FCSTD DOCUMENT  (FreeCAD 0.22R33909 (Git))
Label: milling_vacuum
License: All rights reserved
LicenseURL: http://en.wikipedia.org/wiki/All_rights_reserved
objects: Sketcher::SketchObject×2, PartDesign::Body×1
note: 3 computed .brp shape members not serialized (recipe doc carries the construction recipe); baked Part::Feature solids carry a one-line shape summary decoded from their .brp

FEATURE [Sketcher::SketchObject] Sketch
  FullyConstrained = true
  MapMode = 5
  Support = -> [XY_Plane]
  sketch-geometry (1):
    g0: Circle CenterX=0 CenterY=0 CenterZ=0 NormalX=0 NormalY=0 NormalZ=1 AngleXU=0 Radius=38.5
  constraints (2):
    c: Coincident(g0,g-1)
    c: Diameter(g0) = 77
FEATURE [Sketcher::SketchObject] Sketch001
  AttachmentOffset = pos=(0,0,46) rot=(0,0,1;0rad)
  FullyConstrained = true
  MapMode = 5
  Placement = pos=(0,-46,-1.02e-14) rot=(1,0,0;1.5708rad)
  Support = -> [XZ_Plane]
  sketch-geometry (8):
    g0: ArcOfCircle CenterX=61 CenterY=12 CenterZ=0 NormalX=0 NormalY=0 NormalZ=1 AngleXU=0 Radius=3 StartAngle=3.14159 EndAngle=6.28319
    g1: ArcOfCircle CenterX=61 CenterY=72 CenterZ=0 NormalX=0 NormalY=0 NormalZ=1 AngleXU=0 Radius=3 StartAngle=0 EndAngle=3.14159
    g2: LineSegment StartX=64 StartY=12 StartZ=0 EndX=64 EndY=72 EndZ=0
    g3: LineSegment StartX=58 StartY=72 StartZ=0 EndX=58 EndY=12 EndZ=0
    g4: ArcOfCircle CenterX=-61 CenterY=12 CenterZ=0 NormalX=0 NormalY=0 NormalZ=1 AngleXU=0 Radius=3 StartAngle=3.14159 EndAngle=6.28319
    g5: ArcOfCircle CenterX=-61 CenterY=72 CenterZ=0 NormalX=0 NormalY=0 NormalZ=1 AngleXU=0 Radius=3 StartAngle=1.5e-15 EndAngle=3.14159
    g6: LineSegment StartX=-58 StartY=12 StartZ=0 EndX=-58 EndY=72 EndZ=0
    g7: LineSegment StartX=-64 StartY=72 StartZ=0 EndX=-64 EndY=12 EndZ=0
  constraints (18):
    c: Tangent(g0,g2) = -1.5708
    c: Tangent(g2,g1) = -1.5708
    c: Tangent(g1,g3) = -1.5708
    c: Tangent(g3,g0) = -1.5708
    c: Equal(g0,g1)
    c: Vertical(g2)
    c: Tangent(g4,g6) = -1.5708
    c: Tangent(g6,g5) = -1.5708
    c: Tangent(g5,g7) = -1.5708
    c: Tangent(g7,g4) = -1.5708
    c: Equal(g4,g5)
    c: Equal(g4,g0)
    c: Symmetric(g4,g0,g-2)
    c: Symmetric(g5,g1,g-2)
    c: DistanceX(g4,g0) = 122
    c: Diameter(g0) = 6
    c: DistanceY(g0) = 12
    c: DistanceY(g0,g1) = 60
FEATURE [PartDesign::Body] Body
  Group = -> [Sketch,Sketch001]
  Origin = -> Origin
